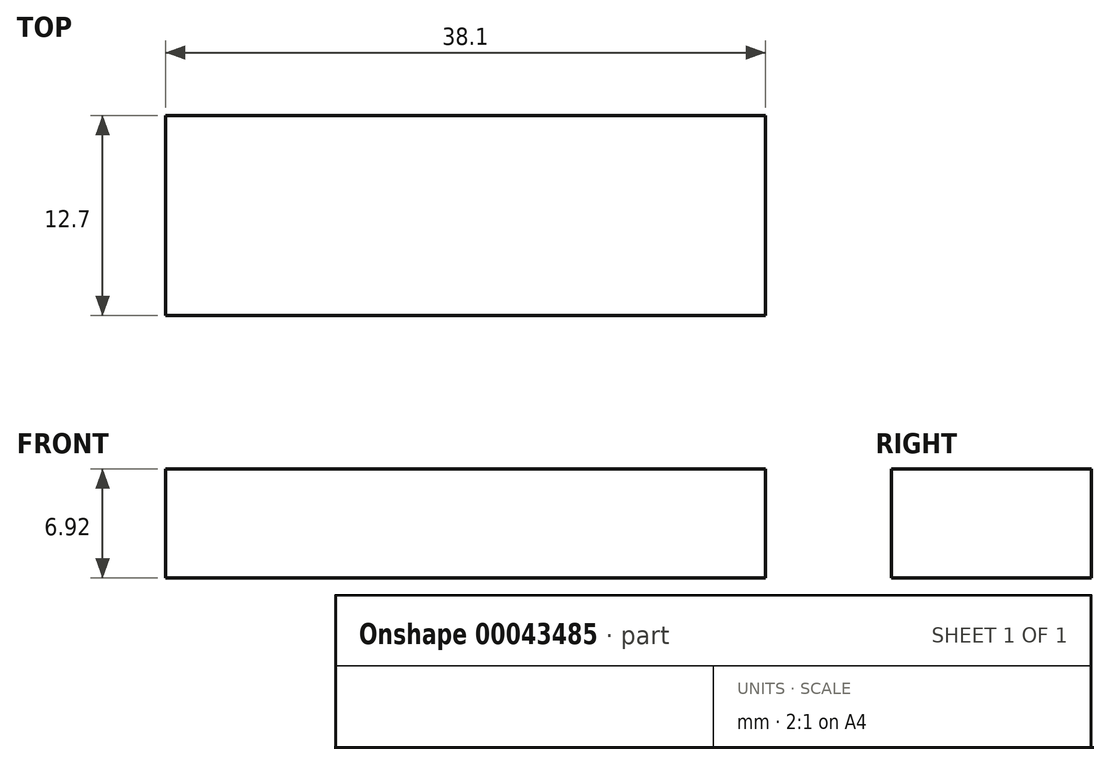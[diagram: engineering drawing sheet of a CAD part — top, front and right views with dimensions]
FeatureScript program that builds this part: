
annotation { "Feature Type Name" : "Feature", "Feature Type Description" : "" }
export const myFeature = defineFeature(function(context is Context, id is Id, definition is map)
    precondition{}
    {
        {
            var Q0;
            Q0=qCreatedBy(makeId("Front.planeOp"),FACE);
            var sketch = newSketch(context, id + "F0", { "sketchPlane" : qUnion([Q0])});
            skLineSegment(sketch, "E0", {"start": v(-18.88, 27.37) * mm, "end": v(19.22, 27.37) * mm});
            skLineSegment(sketch, "E1", {"start": v(19.22, 27.37) * mm, "end": v(19.22, 20.45) * mm});
            skLineSegment(sketch, "E2", {"start": v(19.22, 20.45) * mm, "end": v(-18.88, 20.45) * mm});
            skLineSegment(sketch, "E3", {"start": v(-18.88, 20.45) * mm, "end": v(-18.88, 27.37) * mm});
            skSolve(sketch);
        }
        {
            var Q0;
            Q0 = qSketchRegion(id + "F0", true);
            extrude(context, id + "F1", {"entities" : qUnion([Q0]), "depth" : 12.7 * mm});
        }
    });
